# Revit family: ledspotra-chiara-e_9w-dim-930-36d-wh_541003589300
name_source: partatom
category: Lighting Fixtures
units: mm (PartAtom-declared; Revit-internal decimal feet)

## family parameters
Cut with Voids When Loaded = No
Host = Face
Light Source = No
Part Type = Normal
Room Calculation Point = No
Round Connector Dimension = Use Diameter
Shared = No

## types (1)
- LEDSpotRA-Chiara-E 9W-DIM-930-36D-WH (1 x LED, 675 lm, 3000)
    Apparent Load = 9 VA
    Approval mark = CE
    CIE Flux Codes = 93 97 99 100 100
    Color Rendering = 90
    Color Temperature = 3000
    Control Gear = Electronic ballast
    Default Elevation = 1800 mm
    Description = Recessed LED spot with 25° tilting angle. Clean beam thanks to newly designed micro faceted reflector. Light free of multiple shadows for professional accent lighting. Universal cut-out of 68mm. IP44 on the light emitting side.
    Frequency = 60 Hz
    Height = 0 mm  [stored 0 ft]
    Lamp = 1 x LED
    Lamp Light Flux = 675 lm
    Lamp count = 1
    Length = 83 mm
    Luminous efficacy = 75 lm/W
    Manufacturer = OPPLE
    ModVariant = No
    Model = 541003589300
    Mounting Place = Ceiling, Pole
    Mounting Type = Recessed
    Number of Poles = 1
    OnlyDefault = Yes
    Power Factor = 1
    Product Name = LEDSpotRA-Chiara-E 9W-DIM-930-36D-WH
    Product group = Spot Chiara
    ProductGroupID = 430
    Protection Class = Protection class II
    Protection Degree = IP 44
    RLX_Detail_Level = 1
    RlxData = <blob elided: 22909 chars, md5=ef412cb3>
    Socket = socket
    Standby Power = 0 W
    System Light Flux = 675 lm
    System Power = 9 W
    Type Comments = Product without accessories
    Type Image = web_chiara_wh.jpg
    URL = http://relux.com
    VarID = ---
    Voltage = 230 V
    Voltage Range = 220-240 V
    Weight = 0.00 kg
    Width = 83 mm

note: [stored X ft] marks values corroborated as IEEE doubles in the binary element streams (Revit-internal decimal feet)

## geometry (parser evidence)
native form markers: Blend x4, Sweep x10
no freeform markers — native parametric forms only
